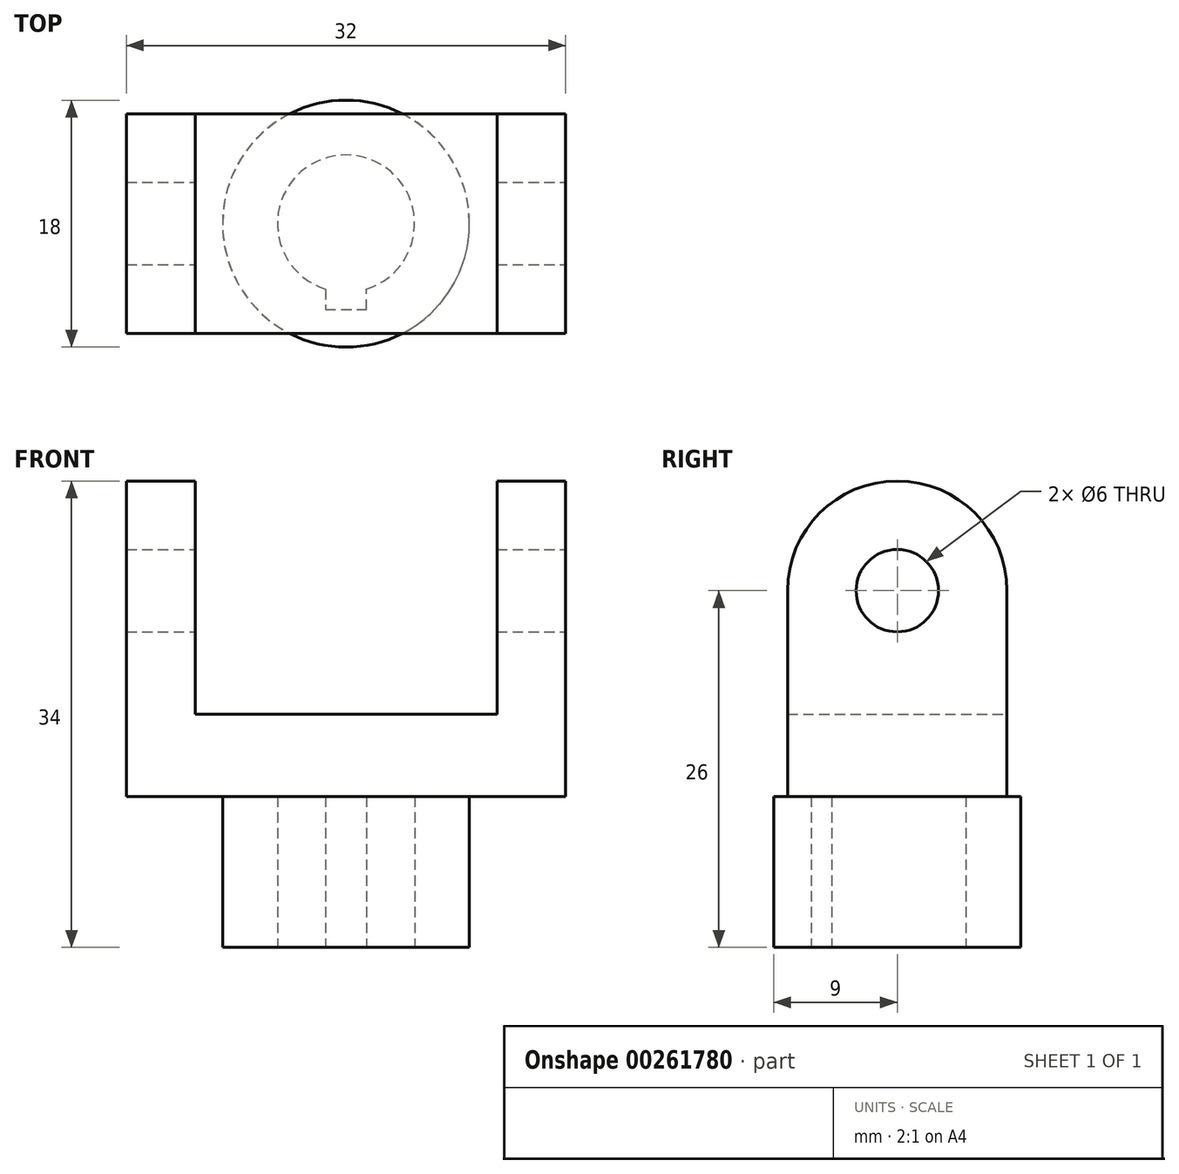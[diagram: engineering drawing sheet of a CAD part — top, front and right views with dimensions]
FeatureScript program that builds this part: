
annotation { "Feature Type Name" : "Feature", "Feature Type Description" : "" }
export const myFeature = defineFeature(function(context is Context, id is Id, definition is map)
    precondition{}
    {
        {
            var Q0;
            Q0=qCreatedBy(makeId("Front.planeOp"),FACE);
            var sketch = newSketch(context, id + "F0", { "sketchPlane" : qUnion([Q0])});
            skLineSegment(sketch, "E0", {"start": v(0, 0) * mm, "end": v(32, 0) * mm});
            skLineSegment(sketch, "E1", {"start": v(32, 0) * mm, "end": v(32, 23) * mm});
            skLineSegment(sketch, "E2", {"start": v(32, 23) * mm, "end": v(27, 23) * mm});
            skLineSegment(sketch, "E3", {"start": v(27, 23) * mm, "end": v(27, 6) * mm});
            skLineSegment(sketch, "E4", {"start": v(27, 6) * mm, "end": v(5, 6) * mm});
            skLineSegment(sketch, "E5", {"start": v(5, 6) * mm, "end": v(5, 23) * mm});
            skLineSegment(sketch, "E6", {"start": v(5, 23) * mm, "end": v(0, 23) * mm});
            skLineSegment(sketch, "E7", {"start": v(0, 23) * mm, "end": v(0, 0) * mm});
            skLineSegment(sketch, "E8", {"start": v(16, 0) * mm, "end": v(16, -11) * mm});
            skLineSegment(sketch, "E9", {"start": v(16, -11) * mm, "end": v(7, -11) * mm});
            skLineSegment(sketch, "E10", {"start": v(7, -11) * mm, "end": v(7, 0) * mm});
            skSolve(sketch);
        }
        {
            var Q0;
            {var subQ0=sQuery(id+"F0.wireOp",EDGE,"E8");Q0=makeQuery(id+"F0.imprint","IMPRINT",FACE,{"disambiguationData":[TD([[makeQuery(id+"F0.imprint","IMPRINT",EDGE,{"derivedFrom":subQ0}),-1.0]])]});}
            var Q1;
            Q1=sQuery(id+"F0.wireOp",EDGE,"E8");
            revolve(context, id + "F1", {"entities" : qUnion([Q0]), "axis" : qUnion([Q1]), "revolveType" : RevolveType.FULL});
        }
        {
            var Q0;
            Q0 = qSketchRegion(id + "FJ9KJaCrt9Enqb2_0", true);
            var Q1;
            {var subQ0=sQuery(id+"F0.wireOp",EDGE,"E1");Q1=makeQuery(id+"F0.imprint","IMPRINT",FACE,{"disambiguationData":[TD([[makeQuery(id+"F0.imprint","IMPRINT",EDGE,{"derivedFrom":subQ0}),1.0]])]});}
            extrude(context, id + "F2", {"entities" : qUnion([Q0, Q1]), "operationType" : NewBodyOperationType.ADD, "endBound" : BoundingType.SYMMETRIC, "depth" : 16 * mm});
        }
        {
            var Q0;
            Q0=makeQuery(id+"F1.opRevolve","SWEPT_FACE",FACE,{"disambiguationData":[OSD([sQuery(id+"F0.wireOp",EDGE,"E9")])]});
            var sketch = newSketch(context, id + "F3", { "sketchPlane" : qUnion([Q0])});
            skArc(sketch, "E11", {"start": v(14.5, 4.77) * mm, "mid": v(16, -5) * mm, "end": v(17.5, 4.77) * mm});
            skLineSegment(sketch, "E12", {"start": v(14.5, 4.77) * mm, "end": v(14.5, 6.27) * mm});
            skLineSegment(sketch, "E13", {"start": v(14.5, 6.27) * mm, "end": v(17.5, 6.27) * mm});
            skLineSegment(sketch, "E14", {"start": v(17.5, 6.27) * mm, "end": v(17.5, 4.77) * mm});
            skLineSegment(sketch, "E15", {"start": v(16, 6.27) * mm, "end": v(16, 15.34) * mm, "construction": true});
            skSolve(sketch);
        }
        {
            var Q0;
            Q0=makeQuery(id+"F3.imprint","IMPRINT",FACE,{"disambiguationData":[TD([[makeQuery(id+"F3.imprint","IMPRINT",EDGE,{"derivedFrom":sQuery(id+"F3.wireOp",EDGE,"E11")}),1.0]])]});
            extrude(context, id + "F4", {"entities" : qUnion([Q0]), "operationType" : NewBodyOperationType.REMOVE, "oppositeDirection" : true, "depth" : 11 * mm});
        }
        {
            var Q0;
            Q0=makeQuery(id+"F2.opExtrude","SWEPT_FACE",FACE,{"disambiguationData":[OSD([sQuery(id+"F0.wireOp",EDGE,"E1")])]});
            var sketch = newSketch(context, id + "F5", { "sketchPlane" : qUnion([Q0])});
            skCircle(sketch, "E16", {"center": v(0, 15) * mm, "radius": 3 * mm});
            skArc(sketch, "E17", {"start": v(8, 15) * mm, "mid": v(0, 23) * mm, "end": v(-8, 15) * mm});
            skLineSegment(sketch, "E18.0", {"start": v(-8, 15) * mm, "end": v(-8, 23) * mm});
            skLineSegment(sketch, "E19.0", {"start": v(-8, 23) * mm, "end": v(8, 23) * mm});
            skLineSegment(sketch, "E20.0", {"start": v(8, 0) * mm, "end": v(8, 23) * mm});
            skPoint(sketch, "E21.orphan", {"position": v(-8, 0) * mm});
            skSolve(sketch);
        }
        {
            var Q0;
            Q0 = qSketchRegion(id + "F5", true);
            extrude(context, id + "F6", {"entities" : qUnion([Q0]), "operationType" : NewBodyOperationType.REMOVE, "endBound" : BoundingType.THROUGH_ALL, "oppositeDirection" : true, "depth" : 25 * mm});
        }
    });
